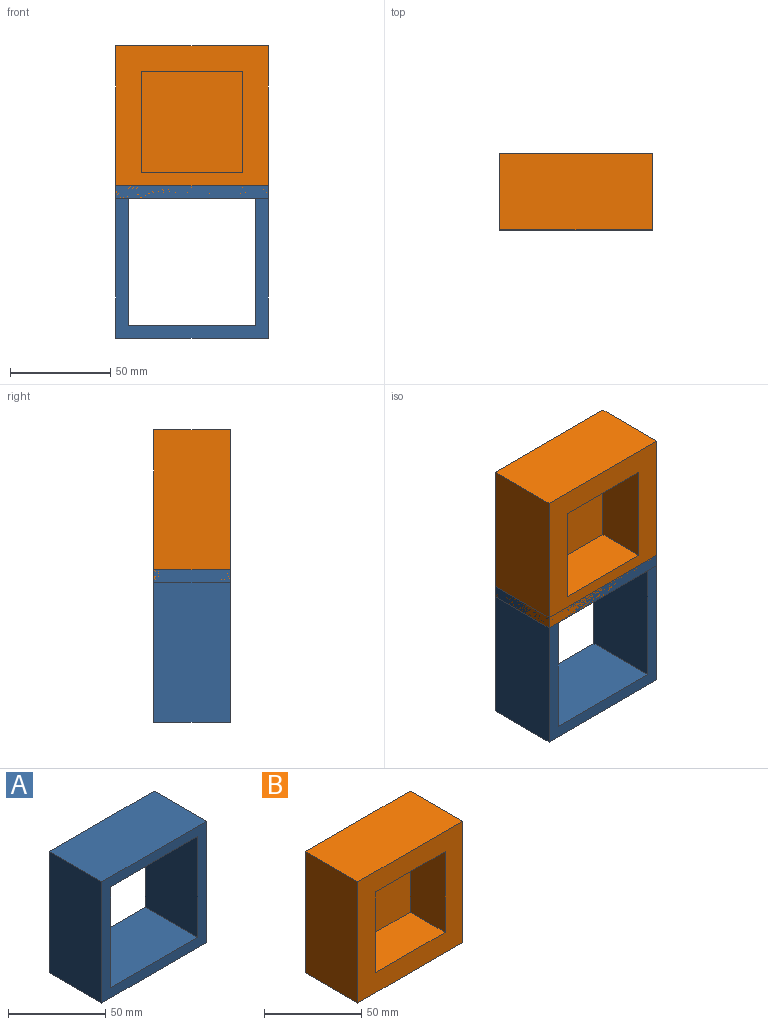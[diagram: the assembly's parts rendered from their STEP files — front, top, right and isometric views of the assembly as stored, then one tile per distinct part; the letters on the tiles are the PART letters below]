
ASSEMBLY  parts=2 mates=1
PART A: 10 faces, bbox 76.2x38.1x76.2 mm
  f0: plane 76.2x38.1mm, normal (1,0,0), area 2903.2mm2, adj f1,f7,f8,f9
  f1: plane 76.2x38.1mm, normal (0,0,1), area 2903.2mm2, adj f0,f2,f8,f9
  f2: plane 76.2x38.1mm, normal (-1,0,0), area 2903.2mm2, adj f1,f7,f8,f9
  f3: plane 63.5x38.1mm, normal (0,0,-1), area 2419.3mm2, adj f4,f6,f8,f9
  f4: plane 63.5x38.1mm, normal (-1,0,0), area 2419.3mm2, adj f3,f5,f8,f9
  f5: plane 63.5x38.1mm, normal (0,0,1), area 2419.3mm2, adj f4,f6,f8,f9
  f6: plane 63.5x38.1mm, normal (1,0,0), area 2419.3mm2, adj f3,f5,f8,f9
  f7: plane 76.2x38.1mm, normal (0,0,-1), area 2903.2mm2, adj f0,f2,f8,f9
  f8: plane 76.2x76.2mm, normal (0,-1,0), area 1774.2mm2, adj f0,f1,f2,f3,f4,f5,f6,f7
  f9: plane 76.2x76.2mm, normal (0,1,0), area 1774.2mm2, adj f0,f1,f2,f3,f4,f5,f6,f7
PART B: 11 faces, bbox 76.2x38.1x76.2 mm
  f0: plane 76.2x38.1mm, normal (1,0,0), area 2903.2mm2, adj f1,f3,f4,f5
  f1: plane 76.2x38.1mm, normal (0,0,1), area 2903.2mm2, adj f0,f2,f4,f5
  f2: plane 76.2x38.1mm, normal (-1,0,0), area 2903.2mm2, adj f1,f3,f4,f5
  f3: plane 76.2x38.1mm, normal (0,0,-1), area 2903.2mm2, adj f0,f2,f4,f5
  f4: plane 76.2x76.2mm, normal (0,-1,0), area 3225.8mm2, adj f0,f1,f2,f3,f6,f7,f8,f9
  f5: plane 76.2x76.2mm, normal (0,1,0), area 5806.4mm2, adj f0,f1,f2,f3
  f6: plane 50.8x25.4mm, normal (-1,0,0), area 1290.3mm2, adj f4,f7,f9,f10
  f7: plane 50.8x25.4mm, normal (0,0,-1), area 1290.3mm2, adj f4,f6,f8,f10
  f8: plane 50.8x25.4mm, normal (1,0,0), area 1290.3mm2, adj f4,f7,f9,f10
  f9: plane 50.8x25.4mm, normal (0,0,1), area 1290.3mm2, adj f4,f6,f8,f10
  f10: plane 50.8x50.8mm, normal (0,-1,0), area 2580.6mm2, adj f6,f7,f8,f9
PLACE A rot(axis=(1,0,0),180deg) t=(-65.92,-66.92,-85.89)mm
PLACE B t=(-65.92,-28.82,-16.04)mm
MATE ball B.f3 <-> A.f5  axis (0,0,-1) through (-65.92,-47.87,-54.14)mm
